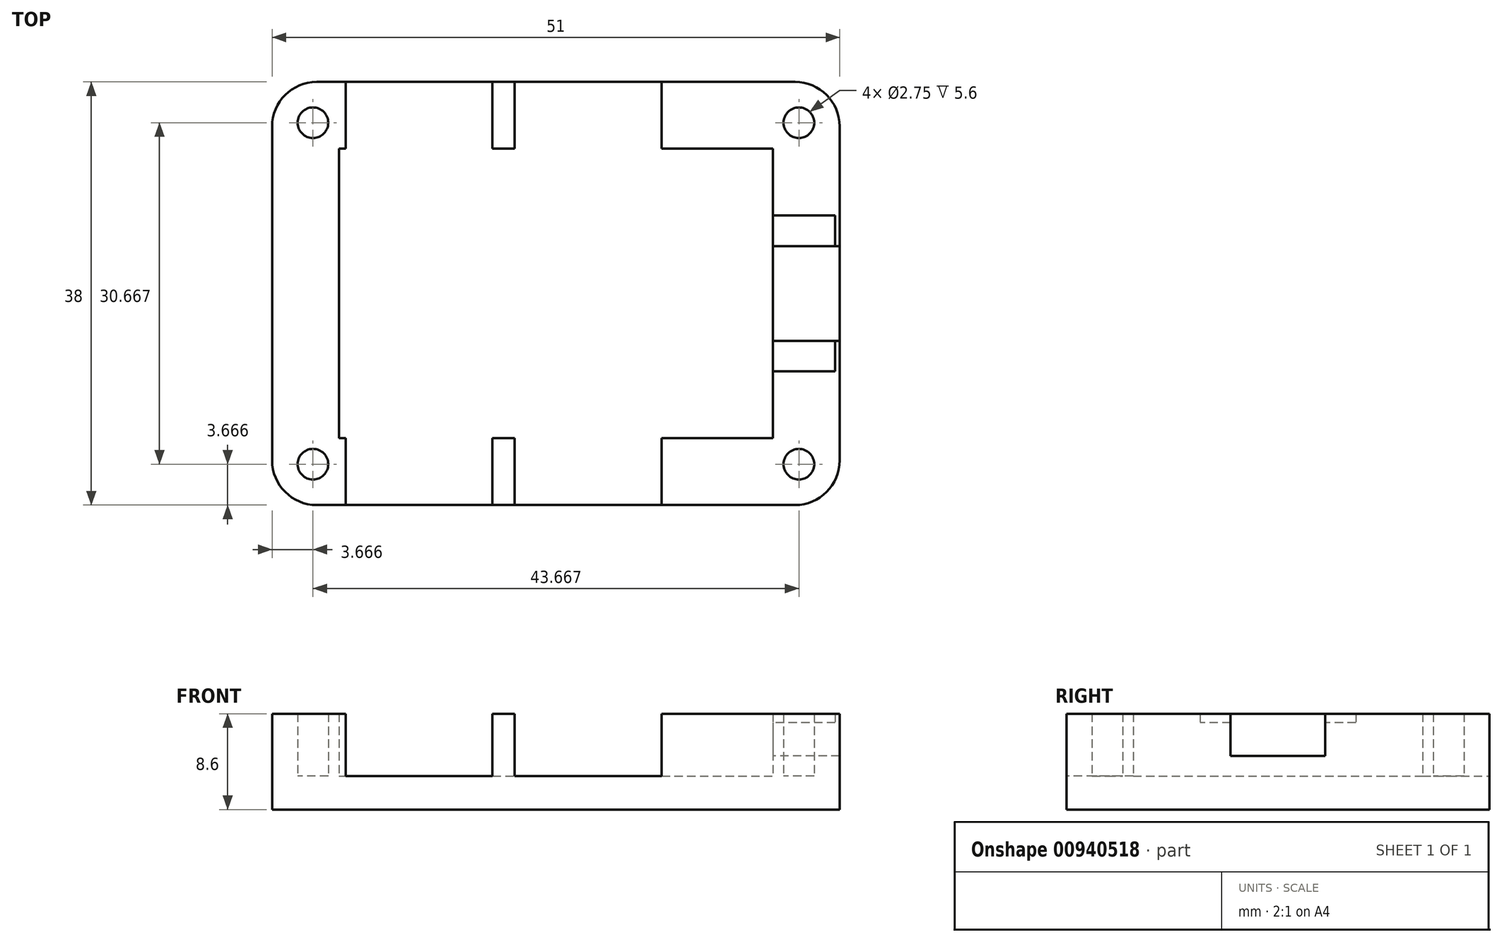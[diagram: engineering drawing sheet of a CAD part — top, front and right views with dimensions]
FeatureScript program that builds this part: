
annotation { "Feature Type Name" : "Feature", "Feature Type Description" : "" }
export const myFeature = defineFeature(function(context is Context, id is Id, definition is map)
    precondition{}
    {
        {
            var Q0;
            Q0=qCreatedBy(makeId("Top.planeOp"),FACE);
            var sketch = newSketch(context, id + "F0", { "sketchPlane" : qUnion([Q0])});
            skLineSegment(sketch, "E0.bottom", {"start": v(21.5, 19) * mm, "end": v(-21.5, 19) * mm});
            skLineSegment(sketch, "E0.top", {"start": v(21.5, -19) * mm, "end": v(-21.5, -19) * mm});
            skLineSegment(sketch, "E0.left", {"start": v(25.5, 15) * mm, "end": v(25.5, -15) * mm});
            skLineSegment(sketch, "E0.right", {"start": v(-25.5, 15) * mm, "end": v(-25.5, -15) * mm});
            skPoint(sketch, "E0.middle", {"position": v(0, 0) * mm});
            skLineSegment(sketch, "E1.bottom", {"start": v(19.5, 13) * mm, "end": v(-19.5, 13) * mm});
            skLineSegment(sketch, "E1.top", {"start": v(19.5, -13) * mm, "end": v(-19.5, -13) * mm});
            skLineSegment(sketch, "E1.left", {"start": v(19.5, 13) * mm, "end": v(19.5, -13) * mm});
            skLineSegment(sketch, "E1.right", {"start": v(-19.5, 13) * mm, "end": v(-19.5, -13) * mm});
            skLineSegment(sketch, "E2", {"start": v(19.5, 0) * mm, "end": v(25.5, 0) * mm, "construction": true});
            skLineSegment(sketch, "E3.bottom", {"start": v(25.5, 7) * mm, "end": v(19.5, 7) * mm});
            skLineSegment(sketch, "E3.top", {"start": v(25.5, -7) * mm, "end": v(19.5, -7) * mm});
            skLineSegment(sketch, "E3.left", {"start": v(25.5, 7) * mm, "end": v(25.5, -7) * mm});
            skLineSegment(sketch, "E3.right", {"start": v(19.5, 7) * mm, "end": v(19.5, -7) * mm});
            skPoint(sketch, "E3.middle", {"position": v(22.5, 0) * mm});
            skLineSegment(sketch, "E4", {"start": v(25.1, 7) * mm, "end": v(25.1, -7) * mm});
            skLineSegment(sketch, "E5.bottom", {"start": v(25.5, 4.25) * mm, "end": v(19.5, 4.25) * mm});
            skLineSegment(sketch, "E5.top", {"start": v(25.5, -4.25) * mm, "end": v(19.5, -4.25) * mm});
            skLineSegment(sketch, "E5.left", {"start": v(25.5, 4.25) * mm, "end": v(25.5, -4.25) * mm});
            skLineSegment(sketch, "E5.right", {"start": v(19.5, 4.25) * mm, "end": v(19.5, -4.25) * mm});
            skLineSegment(sketch, "E6", {"start": v(9.5, 19) * mm, "end": v(9.5, 13) * mm});
            skLineSegment(sketch, "E7", {"start": v(-3.7, 19) * mm, "end": v(-3.7, 13) * mm});
            skLineSegment(sketch, "E8", {"start": v(-5.7, 19) * mm, "end": v(-5.7, 13) * mm});
            skLineSegment(sketch, "E9", {"start": v(-18.9, 19) * mm, "end": v(-18.9, 13) * mm});
            skPoint(sketch, "E10.visualSharp", {"position": v(-25.5, 19) * mm});
            skArc(sketch, "E10.filletArc", {"start": v(-21.5, 19) * mm, "mid": v(-24.33, 17.83) * mm, "end": v(-25.5, 15) * mm});
            skPoint(sketch, "E11.visualSharp", {"position": v(-25.5, -19) * mm});
            skArc(sketch, "E11.filletArc", {"start": v(-25.5, -15) * mm, "mid": v(-24.33, -17.83) * mm, "end": v(-21.5, -19) * mm});
            skPoint(sketch, "E12.visualSharp", {"position": v(25.5, -19) * mm});
            skArc(sketch, "E12.filletArc", {"start": v(21.5, -19) * mm, "mid": v(24.33, -17.83) * mm, "end": v(25.5, -15) * mm});
            skPoint(sketch, "E13.visualSharp", {"position": v(25.5, 19) * mm});
            skArc(sketch, "E13.filletArc", {"start": v(25.5, 15) * mm, "mid": v(24.33, 17.83) * mm, "end": v(21.5, 19) * mm});
            skLineSegment(sketch, "E14", {"start": v(19.5, 13) * mm, "end": v(25.5, 19) * mm, "construction": true});
            skCircle(sketch, "E15", {"center": v(21.83, 15.33) * mm, "radius": 2.6 * mm});
            skCircle(sketch, "E16", {"center": v(21.83, 15.33) * mm, "radius": 1.38 * mm});
            skCircle(sketch, "E17", {"center": v(21.83, 15.33) * mm, "radius": 1.55 * mm});
            skCircle(sketch, "E18.0.1.0", {"center": v(21.83, -15.33) * mm, "radius": 2.6 * mm});
            skCircle(sketch, "E18.0.1.1", {"center": v(21.83, -15.33) * mm, "radius": 1.55 * mm});
            skCircle(sketch, "E18.0.1.2", {"center": v(21.83, -15.33) * mm, "radius": 1.38 * mm});
            skCircle(sketch, "E18.1.0.0", {"center": v(-21.83, 15.33) * mm, "radius": 2.6 * mm});
            skCircle(sketch, "E18.1.0.1", {"center": v(-21.83, 15.33) * mm, "radius": 1.55 * mm});
            skCircle(sketch, "E18.1.0.2", {"center": v(-21.83, 15.33) * mm, "radius": 1.38 * mm});
            skCircle(sketch, "E18.1.1.0", {"center": v(-21.83, -15.33) * mm, "radius": 2.6 * mm});
            skCircle(sketch, "E18.1.1.1", {"center": v(-21.83, -15.33) * mm, "radius": 1.55 * mm});
            skCircle(sketch, "E18.1.1.2", {"center": v(-21.83, -15.33) * mm, "radius": 1.38 * mm});
            skLineSegment(sketch, "E18.direction1", {"start": v(21.83, 15.33) * mm, "end": v(-21.83, 15.33) * mm, "construction": true});
            skLineSegment(sketch, "E18.direction2", {"start": v(21.83, 15.33) * mm, "end": v(21.83, -15.33) * mm, "construction": true});
            skLineSegment(sketch, "E19", {"start": v(-19.5, 13) * mm, "end": v(-25.5, 19) * mm, "construction": true});
            skLineSegment(sketch, "E20", {"start": v(19.5, -13) * mm, "end": v(25.5, -19) * mm, "construction": true});
            skLineSegment(sketch, "E21.MirrorCS", {"start": v(9.5, -19) * mm, "end": v(9.5, -13) * mm});
            skLineSegment(sketch, "E22.MirrorCS", {"start": v(-3.7, -19) * mm, "end": v(-3.7, -13) * mm});
            skLineSegment(sketch, "E23.MirrorCS", {"start": v(-5.7, -19) * mm, "end": v(-5.7, -13) * mm});
            skLineSegment(sketch, "E24.MirrorCS", {"start": v(-18.9, -19) * mm, "end": v(-18.9, -13) * mm});
            skSolve(sketch);
        }
        {
            var Q0;
            {var subQ6=sQuery(id+"F0.wireOp",EDGE,"E12.filletArc");Q0=makeQuery(id+"F0.imprint","IMPRINT",FACE,{"disambiguationData":[TD([[makeQuery(id+"F0.imprint","IMPRINT",EDGE,{"derivedFrom":subQ6}),1.0]])]});}
            var Q1;
            {var subQ0=sQuery(id+"F0.wireOp",EDGE,"E5.bottom");var subQ1=sQuery(id+"F0.wireOp",EDGE,"E1.left");var subQ2=makeQuery(id+"F0.imprint","INTERSECT",VERTEX,{"derivedFrom":[subQ1,subQ0]});Q1=makeQuery(id+"F0.imprint","IMPRINT",FACE,{"disambiguationData":[TD([[makeQuery(id+"F0.imprint","IMPRINT",EDGE,{"disambiguationData":[TD([[subQ2,1.0]])],"derivedFrom":subQ1}),1.0]])]});}
            var Q2;
            Q2=makeQuery(id+"F0.imprint","IMPRINT",FACE,{"disambiguationData":[TD([[makeQuery(id+"F0.imprint","IMPRINT",EDGE,{"derivedFrom":sQuery(id+"F0.wireOp",EDGE,"E18.1.1.2")}),1.0]])]});
            var Q3;
            Q3=makeQuery(id+"F0.imprint","IMPRINT",FACE,{"disambiguationData":[TD([[makeQuery(id+"F0.imprint","IMPRINT",EDGE,{"derivedFrom":sQuery(id+"F0.wireOp",EDGE,"E18.1.1.0")}),1.0]])]});
            var Q4;
            Q4=makeQuery(id+"F0.imprint","IMPRINT",FACE,{"disambiguationData":[TD([[makeQuery(id+"F0.imprint","IMPRINT",EDGE,{"derivedFrom":sQuery(id+"F0.wireOp",EDGE,"E15")}),1.0]])]});
            var Q5;
            {var subQ0=sQuery(id+"F0.wireOp",EDGE,"E23.MirrorCS");Q5=makeQuery(id+"F0.imprint","IMPRINT",FACE,{"disambiguationData":[TD([[makeQuery(id+"F0.imprint","IMPRINT",EDGE,{"derivedFrom":subQ0}),1.0]])]});}
            var Q6;
            Q6=makeQuery(id+"F0.imprint","IMPRINT",FACE,{"disambiguationData":[TD([[makeQuery(id+"F0.imprint","IMPRINT",EDGE,{"derivedFrom":sQuery(id+"F0.wireOp",EDGE,"E18.1.0.0")}),1.0]])]});
            var Q7;
            {var subQ0=sQuery(id+"F0.wireOp",EDGE,"E6");Q7=makeQuery(id+"F0.imprint","IMPRINT",FACE,{"disambiguationData":[TD([[makeQuery(id+"F0.imprint","IMPRINT",EDGE,{"derivedFrom":subQ0}),-1.0]])]});}
            var Q8;
            Q8=makeQuery(id+"F0.imprint","IMPRINT",FACE,{"disambiguationData":[TD([[makeQuery(id+"F0.imprint","IMPRINT",EDGE,{"derivedFrom":sQuery(id+"F0.wireOp",EDGE,"E18.1.0.2")}),1.0]])]});
            var Q9;
            Q9=makeQuery(id+"F0.imprint","IMPRINT",FACE,{"disambiguationData":[TD([[makeQuery(id+"F0.imprint","IMPRINT",EDGE,{"derivedFrom":sQuery(id+"F0.wireOp",EDGE,"E0.right")}),1.0]])]});
            var Q10;
            {var subQ0=sQuery(id+"F0.wireOp",EDGE,"E8");Q10=makeQuery(id+"F0.imprint","IMPRINT",FACE,{"disambiguationData":[TD([[makeQuery(id+"F0.imprint","IMPRINT",EDGE,{"derivedFrom":subQ0}),-1.0]])]});}
            var Q11;
            {var subQ0=sQuery(id+"F0.wireOp",EDGE,"E21.MirrorCS");Q11=makeQuery(id+"F0.imprint","IMPRINT",FACE,{"disambiguationData":[TD([[makeQuery(id+"F0.imprint","IMPRINT",EDGE,{"derivedFrom":subQ0}),1.0]])]});}
            var Q12;
            {var subQ2=sQuery(id+"F0.wireOp",EDGE,"E22.MirrorCS");Q12=makeQuery(id+"F0.imprint","IMPRINT",FACE,{"disambiguationData":[TD([[makeQuery(id+"F0.imprint","IMPRINT",EDGE,{"derivedFrom":subQ2}),1.0]])]});}
            var Q13;
            {var subQ0=sQuery(id+"F0.wireOp",EDGE,"E5.top");var subQ1=sQuery(id+"F0.wireOp",EDGE,"E1.left");var subQ2=makeQuery(id+"F0.imprint","INTERSECT",VERTEX,{"derivedFrom":[subQ1,subQ0]});Q13=makeQuery(id+"F0.imprint","IMPRINT",FACE,{"disambiguationData":[TD([[makeQuery(id+"F0.imprint","IMPRINT",EDGE,{"disambiguationData":[TD([[subQ2,-1.0]])],"derivedFrom":subQ1}),1.0]])]});}
            var Q14;
            {var subQ2=sQuery(id+"F0.wireOp",EDGE,"E7");Q14=makeQuery(id+"F0.imprint","IMPRINT",FACE,{"disambiguationData":[TD([[makeQuery(id+"F0.imprint","IMPRINT",EDGE,{"derivedFrom":subQ2}),-1.0]])]});}
            var Q15;
            {var subQ0=sQuery(id+"F0.wireOp",EDGE,"E6");Q15=makeQuery(id+"F0.imprint","IMPRINT",FACE,{"disambiguationData":[TD([[makeQuery(id+"F0.imprint","IMPRINT",EDGE,{"derivedFrom":subQ0}),1.0]])]});}
            var Q16;
            Q16=makeQuery(id+"F0.imprint","IMPRINT",FACE,{"disambiguationData":[TD([[makeQuery(id+"F0.imprint","IMPRINT",EDGE,{"derivedFrom":sQuery(id+"F0.wireOp",EDGE,"E18.0.1.0")}),1.0]])]});
            var Q17;
            {var subQ0=sQuery(id+"F0.wireOp",EDGE,"E1.right");Q17=makeQuery(id+"F0.imprint","IMPRINT",FACE,{"disambiguationData":[TD([[makeQuery(id+"F0.imprint","IMPRINT",EDGE,{"derivedFrom":subQ0}),1.0]])]});}
            var Q18;
            {var subQ0=sQuery(id+"F0.wireOp",EDGE,"E5.bottom");var subQ1=sQuery(id+"F0.wireOp",EDGE,"E1.left");var subQ2=makeQuery(id+"F0.imprint","INTERSECT",VERTEX,{"derivedFrom":[subQ1,subQ0]});Q18=makeQuery(id+"F0.imprint","IMPRINT",FACE,{"disambiguationData":[TD([[makeQuery(id+"F0.imprint","IMPRINT",EDGE,{"disambiguationData":[TD([[subQ2,-1.0]])],"derivedFrom":subQ1}),1.0]])]});}
            var Q19;
            Q19=makeQuery(id+"F0.imprint","IMPRINT",FACE,{"disambiguationData":[TD([[makeQuery(id+"F0.imprint","IMPRINT",EDGE,{"derivedFrom":sQuery(id+"F0.wireOp",EDGE,"E16")}),-1.0]])]});
            var Q20;
            {var subQ0=sQuery(id+"F0.wireOp",EDGE,"E5.bottom");var subQ1=sQuery(id+"F0.wireOp",EDGE,"E0.left");var subQ2=makeQuery(id+"F0.imprint","INTERSECT",VERTEX,{"derivedFrom":[subQ1,subQ0]});Q20=makeQuery(id+"F0.imprint","IMPRINT",FACE,{"disambiguationData":[TD([[makeQuery(id+"F0.imprint","IMPRINT",EDGE,{"disambiguationData":[TD([[subQ2,1.0]])],"derivedFrom":subQ1}),-1.0]])]});}
            var Q21;
            Q21=makeQuery(id+"F0.imprint","IMPRINT",FACE,{"disambiguationData":[TD([[makeQuery(id+"F0.imprint","IMPRINT",EDGE,{"derivedFrom":sQuery(id+"F0.wireOp",EDGE,"E18.1.1.1")}),1.0]])]});
            var Q22;
            {var subQ0=sQuery(id+"F0.wireOp",EDGE,"E5.bottom");var subQ1=sQuery(id+"F0.wireOp",EDGE,"E0.left");var subQ2=makeQuery(id+"F0.imprint","INTERSECT",VERTEX,{"derivedFrom":[subQ1,subQ0]});Q22=makeQuery(id+"F0.imprint","IMPRINT",FACE,{"disambiguationData":[TD([[makeQuery(id+"F0.imprint","IMPRINT",EDGE,{"disambiguationData":[TD([[subQ2,-1.0]])],"derivedFrom":subQ1}),-1.0]])]});}
            var Q23;
            Q23=makeQuery(id+"F0.imprint","IMPRINT",FACE,{"disambiguationData":[TD([[makeQuery(id+"F0.imprint","IMPRINT",EDGE,{"derivedFrom":sQuery(id+"F0.wireOp",EDGE,"E18.0.1.1")}),1.0]])]});
            var Q24;
            {var subQ0=sQuery(id+"F0.wireOp",EDGE,"E5.top");var subQ1=sQuery(id+"F0.wireOp",EDGE,"E0.left");var subQ2=makeQuery(id+"F0.imprint","INTERSECT",VERTEX,{"derivedFrom":[subQ1,subQ0]});Q24=makeQuery(id+"F0.imprint","IMPRINT",FACE,{"disambiguationData":[TD([[makeQuery(id+"F0.imprint","IMPRINT",EDGE,{"disambiguationData":[TD([[subQ2,-1.0]])],"derivedFrom":subQ1}),-1.0]])]});}
            var Q25;
            Q25=makeQuery(id+"F0.imprint","IMPRINT",FACE,{"disambiguationData":[TD([[makeQuery(id+"F0.imprint","IMPRINT",EDGE,{"derivedFrom":sQuery(id+"F0.wireOp",EDGE,"E18.1.0.1")}),1.0]])]});
            var Q26;
            Q26=makeQuery(id+"F0.imprint","IMPRINT",FACE,{"disambiguationData":[TD([[makeQuery(id+"F0.imprint","IMPRINT",EDGE,{"derivedFrom":sQuery(id+"F0.wireOp",EDGE,"E18.0.1.2")}),1.0]])]});
            var Q27;
            Q27=makeQuery(id+"F0.imprint","IMPRINT",FACE,{"disambiguationData":[TD([[makeQuery(id+"F0.imprint","IMPRINT",EDGE,{"derivedFrom":sQuery(id+"F0.wireOp",EDGE,"E16")}),1.0]])]});
            extrude(context, id + "F1", {"entities" : qUnion([Q0, Q1, Q2, Q3, Q4, Q5, Q6, Q7, Q8, Q9, Q10, Q11, Q12, Q13, Q14, Q15, Q16, Q17, Q18, Q19, Q20, Q21, Q22, Q23, Q24, Q25, Q26, Q27]), "depth" : 3 * mm, "offsetDistance" : 25 * mm});
        }
        {
            var Q0;
            {var subQ2=sQuery(id+"F0.wireOp",EDGE,"E22.MirrorCS");Q0=makeQuery(id+"F0.imprint","IMPRINT",FACE,{"disambiguationData":[TD([[makeQuery(id+"F0.imprint","IMPRINT",EDGE,{"derivedFrom":subQ2}),1.0]])]});}
            var Q1;
            Q1=makeQuery(id+"F0.imprint","IMPRINT",FACE,{"disambiguationData":[TD([[makeQuery(id+"F0.imprint","IMPRINT",EDGE,{"derivedFrom":sQuery(id+"F0.wireOp",EDGE,"E0.right")}),1.0]])]});
            var Q2;
            {var subQ2=sQuery(id+"F0.wireOp",EDGE,"E7");Q2=makeQuery(id+"F0.imprint","IMPRINT",FACE,{"disambiguationData":[TD([[makeQuery(id+"F0.imprint","IMPRINT",EDGE,{"derivedFrom":subQ2}),-1.0]])]});}
            var Q3;
            {var subQ0=sQuery(id+"F0.wireOp",EDGE,"E6");Q3=makeQuery(id+"F0.imprint","IMPRINT",FACE,{"disambiguationData":[TD([[makeQuery(id+"F0.imprint","IMPRINT",EDGE,{"derivedFrom":subQ0}),1.0]])]});}
            var Q4;
            {var subQ6=sQuery(id+"F0.wireOp",EDGE,"E12.filletArc");Q4=makeQuery(id+"F0.imprint","IMPRINT",FACE,{"disambiguationData":[TD([[makeQuery(id+"F0.imprint","IMPRINT",EDGE,{"derivedFrom":subQ6}),1.0]])]});}
            var Q5;
            Q5=makeQuery(id+"F0.imprint","IMPRINT",FACE,{"disambiguationData":[TD([[makeQuery(id+"F0.imprint","IMPRINT",EDGE,{"derivedFrom":sQuery(id+"F0.wireOp",EDGE,"E18.0.1.1")}),1.0]])]});
            var Q6;
            Q6=makeQuery(id+"F0.imprint","IMPRINT",FACE,{"disambiguationData":[TD([[makeQuery(id+"F0.imprint","IMPRINT",EDGE,{"derivedFrom":sQuery(id+"F0.wireOp",EDGE,"E18.0.1.0")}),1.0]])]});
            var Q7;
            Q7=makeQuery(id+"F0.imprint","IMPRINT",FACE,{"disambiguationData":[TD([[makeQuery(id+"F0.imprint","IMPRINT",EDGE,{"derivedFrom":sQuery(id+"F0.wireOp",EDGE,"E18.1.1.1")}),1.0]])]});
            var Q8;
            Q8=makeQuery(id+"F0.imprint","IMPRINT",FACE,{"disambiguationData":[TD([[makeQuery(id+"F0.imprint","IMPRINT",EDGE,{"derivedFrom":sQuery(id+"F0.wireOp",EDGE,"E18.1.1.0")}),1.0]])]});
            var Q9;
            Q9=makeQuery(id+"F0.imprint","IMPRINT",FACE,{"disambiguationData":[TD([[makeQuery(id+"F0.imprint","IMPRINT",EDGE,{"derivedFrom":sQuery(id+"F0.wireOp",EDGE,"E18.1.0.0")}),1.0]])]});
            var Q10;
            Q10=makeQuery(id+"F0.imprint","IMPRINT",FACE,{"disambiguationData":[TD([[makeQuery(id+"F0.imprint","IMPRINT",EDGE,{"derivedFrom":sQuery(id+"F0.wireOp",EDGE,"E18.1.0.1")}),1.0]])]});
            var Q11;
            Q11=makeQuery(id+"F0.imprint","IMPRINT",FACE,{"disambiguationData":[TD([[makeQuery(id+"F0.imprint","IMPRINT",EDGE,{"derivedFrom":sQuery(id+"F0.wireOp",EDGE,"E16")}),-1.0]])]});
            var Q12;
            Q12=makeQuery(id+"F0.imprint","IMPRINT",FACE,{"disambiguationData":[TD([[makeQuery(id+"F0.imprint","IMPRINT",EDGE,{"derivedFrom":sQuery(id+"F0.wireOp",EDGE,"E15")}),1.0]])]});
            var Q13;
            {var subQ0=sQuery(id+"F0.wireOp",EDGE,"E5.bottom");var subQ1=sQuery(id+"F0.wireOp",EDGE,"E0.left");var subQ2=makeQuery(id+"F0.imprint","INTERSECT",VERTEX,{"derivedFrom":[subQ1,subQ0]});Q13=makeQuery(id+"F0.imprint","IMPRINT",FACE,{"disambiguationData":[TD([[makeQuery(id+"F0.imprint","IMPRINT",EDGE,{"disambiguationData":[TD([[subQ2,1.0]])],"derivedFrom":subQ1}),-1.0]])]});}
            var Q14;
            {var subQ0=sQuery(id+"F0.wireOp",EDGE,"E5.top");var subQ1=sQuery(id+"F0.wireOp",EDGE,"E0.left");var subQ2=makeQuery(id+"F0.imprint","INTERSECT",VERTEX,{"derivedFrom":[subQ1,subQ0]});Q14=makeQuery(id+"F0.imprint","IMPRINT",FACE,{"disambiguationData":[TD([[makeQuery(id+"F0.imprint","IMPRINT",EDGE,{"disambiguationData":[TD([[subQ2,-1.0]])],"derivedFrom":subQ1}),-1.0]])]});}
            extrude(context, id + "F2", {"entities" : qUnion([Q0, Q1, Q2, Q3, Q4, Q5, Q6, Q7, Q8, Q9, Q10, Q11, Q12, Q13, Q14]), "operationType" : NewBodyOperationType.ADD, "depth" : (3 + 5.6) * mm, "offsetDistance" : 25 * mm});
        }
        {
            var Q0;
            {var subQ0=sQuery(id+"F0.wireOp",EDGE,"E5.top");var subQ1=sQuery(id+"F0.wireOp",EDGE,"E1.left");var subQ2=makeQuery(id+"F0.imprint","INTERSECT",VERTEX,{"derivedFrom":[subQ1,subQ0]});Q0=makeQuery(id+"F0.imprint","IMPRINT",FACE,{"disambiguationData":[TD([[makeQuery(id+"F0.imprint","IMPRINT",EDGE,{"disambiguationData":[TD([[subQ2,-1.0]])],"derivedFrom":subQ1}),1.0]])]});}
            var Q1;
            {var subQ0=sQuery(id+"F0.wireOp",EDGE,"E5.bottom");var subQ1=sQuery(id+"F0.wireOp",EDGE,"E1.left");var subQ2=makeQuery(id+"F0.imprint","INTERSECT",VERTEX,{"derivedFrom":[subQ1,subQ0]});Q1=makeQuery(id+"F0.imprint","IMPRINT",FACE,{"disambiguationData":[TD([[makeQuery(id+"F0.imprint","IMPRINT",EDGE,{"disambiguationData":[TD([[subQ2,1.0]])],"derivedFrom":subQ1}),1.0]])]});}
            extrude(context, id + "F3", {"entities" : qUnion([Q0, Q1]), "operationType" : NewBodyOperationType.ADD, "depth" : (3 + 4.8) * mm, "offsetDistance" : 25 * mm});
        }
        {
            var Q0;
            {var subQ0=sQuery(id+"F0.wireOp",EDGE,"E5.bottom");var subQ1=sQuery(id+"F0.wireOp",EDGE,"E1.left");var subQ2=makeQuery(id+"F0.imprint","INTERSECT",VERTEX,{"derivedFrom":[subQ1,subQ0]});Q0=makeQuery(id+"F0.imprint","IMPRINT",FACE,{"disambiguationData":[TD([[makeQuery(id+"F0.imprint","IMPRINT",EDGE,{"disambiguationData":[TD([[subQ2,-1.0]])],"derivedFrom":subQ1}),1.0]])]});}
            var Q1;
            {var subQ0=sQuery(id+"F0.wireOp",EDGE,"E5.bottom");var subQ1=sQuery(id+"F0.wireOp",EDGE,"E0.left");var subQ2=makeQuery(id+"F0.imprint","INTERSECT",VERTEX,{"derivedFrom":[subQ1,subQ0]});Q1=makeQuery(id+"F0.imprint","IMPRINT",FACE,{"disambiguationData":[TD([[makeQuery(id+"F0.imprint","IMPRINT",EDGE,{"disambiguationData":[TD([[subQ2,-1.0]])],"derivedFrom":subQ1}),-1.0]])]});}
            extrude(context, id + "F4", {"entities" : qUnion([Q0, Q1]), "operationType" : NewBodyOperationType.ADD, "depth" : 4.8 * mm, "offsetDistance" : 25 * mm});
        }
    });
